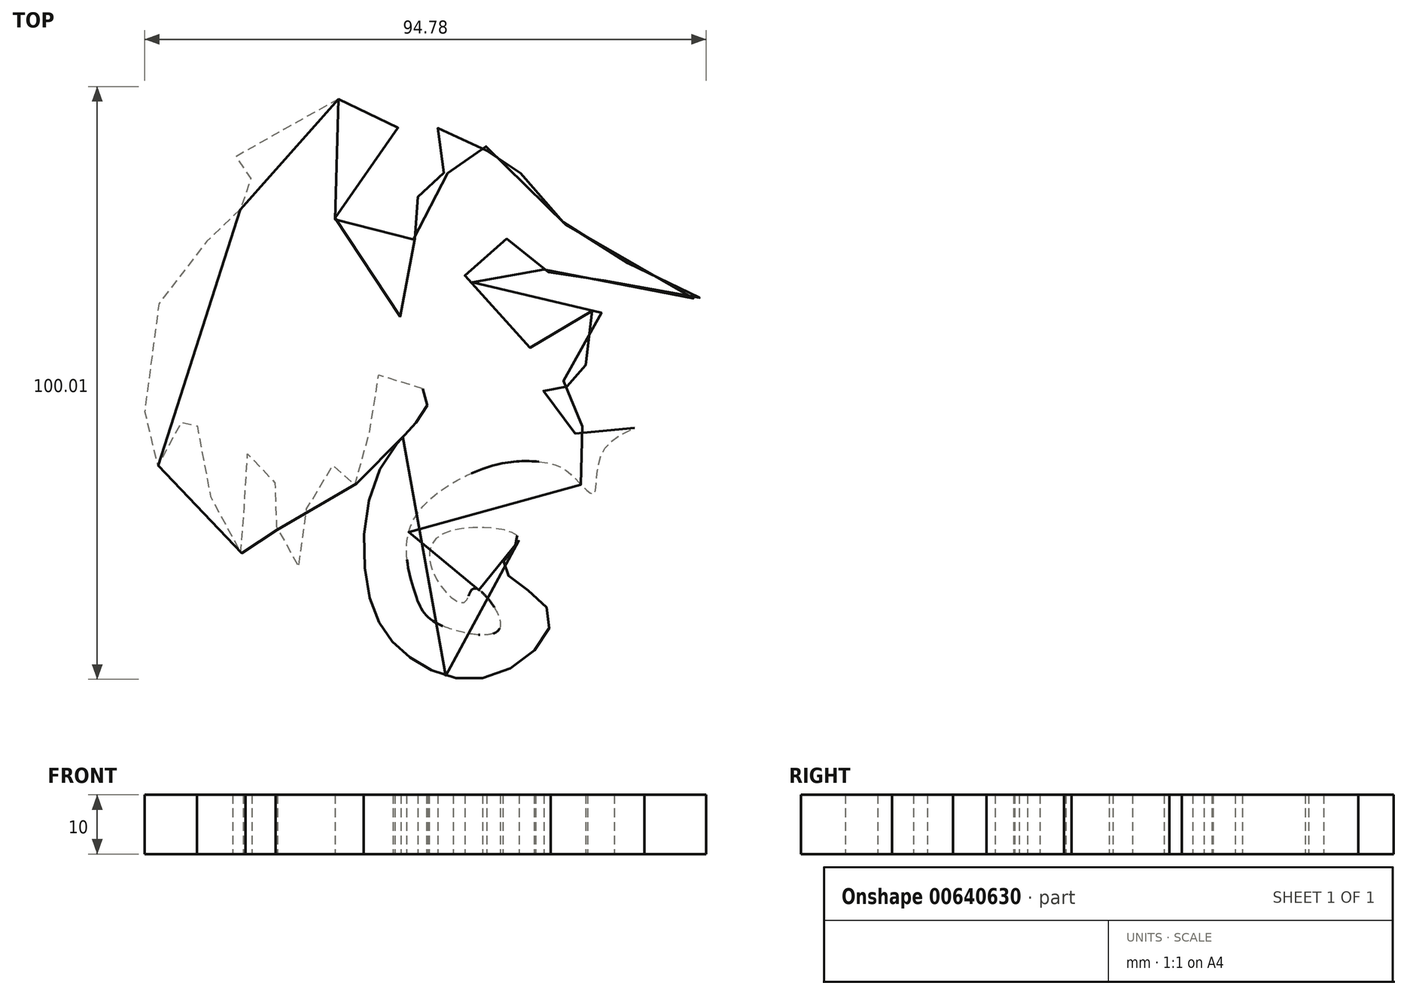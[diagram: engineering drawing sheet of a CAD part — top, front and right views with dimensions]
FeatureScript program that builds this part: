
annotation { "Feature Type Name" : "Feature", "Feature Type Description" : "" }
export const myFeature = defineFeature(function(context is Context, id is Id, definition is map)
    precondition{}
    {
        {
            var Q0;
            Q0=qCreatedBy(makeId("Top.planeOp"),FACE);
            var sketch = newSketch(context, id + "F0", { "sketchPlane" : qUnion([Q0])});
            skFitSpline(sketch, "E0", {"points": [v(-16.96, 41.65) * mm, v(-29.4, 34.76) * mm, v(-34.79, 30.9) * mm, v(-31.76, 28.22) * mm, v(-32.65, 24.68) * mm, v(-35.45, 20.64) * mm, v(-47.4, 6.83) * mm, v(-47.84, -20.41) * mm, v(-43.9, -13.53) * mm, v(-41.16, -11.67) * mm, v(-40.58, -18.2) * mm, v(-33.43, -34.97) * mm, v(-32.93, -26.4) * mm, v(-31.96, -18.08) * mm, v(-27.55, -23.55) * mm, v(-27.43, -30.59) * mm, v(-23.67, -37.29) * mm, v(-21.43, -23.3) * mm, v(-16.96, -20.52) * mm, v(-14.53, -23.54) * mm, v(-11.76, -14.81) * mm, v(-9.4, -4.4) * mm, v(-2, -8.6) * mm, v(-9.07, -19.18) * mm, v(-11.82, -42.06) * mm, v(-4.7, -52.79) * mm, v(9.25, -55.64) * mm, v(18.58, -45) * mm, v(10.74, -37.16) * mm, v(13.45, -32.45) * mm, v(0, -32.12) * mm, v(0, -40.06) * mm, v(4.38, -43.2) * mm, v(5.94, -40.96) * mm, v(10.26, -47.58) * mm, v(0, -47.02) * mm, v(-3.92, -42.22) * mm, v(-4.68, -30.08) * mm, v(8.07, -20.52) * mm, v(16.14, -19.52) * mm, v(20.95, -20.74) * mm, v(24.7, -24.22) * mm, v(26.22, -24.9) * mm, v(28.07, -17.16) * mm, v(34.62, -12.8) * mm, v(26.05, -12.46) * mm, v(21.35, -15.82) * mm, v(16.14, -13.8) * mm, v(17.65, -6.58) * mm, v(16.3, -3.72) * mm, v(19.9, -5.06) * mm, v(21.85, -7.42) * mm, v(23.7, -10.61) * mm, v(25.04, -7.92) * mm, v(25.38, 0) * mm, v(29.58, 3.67) * mm, v(25.21, 5.86) * mm, v(21.35, 2.16) * mm, v(16.64, 0) * mm, v(13.62, 0) * mm, v(7.4, 8.88) * mm, v(2.36, 14.43) * mm, v(6.22, 17.26) * mm, v(12.52, 17.4) * mm, v(13.62, 13.25) * mm, v(16.3, 13.25) * mm, v(19.64, 11.87) * mm, v(23.41, 10.99) * mm, v(26.5, 9.82) * mm, v(28.47, 11.59) * mm, v(37.48, 8.76) * mm, v(45.04, 8.71) * mm, v(39.8, 12.45) * mm, v(28.5, 14.98) * mm, v(24.74, 18.55) * mm, v(20.84, 20.98) * mm, v(19.16, 24.5) * mm, v(16.14, 25.52) * mm, v(12, 32.7) * mm, v(7.4, 37.61) * mm, v(8, 32.04) * mm, v(3.58, 35.75) * mm, v(0, 37.55) * mm, v(1.18, 33.08) * mm, v(4.34, 28.94) * mm, v(-1.84, 29.38) * mm, v(-7.72, 27.53) * mm, v(-3.7, 25.35) * mm, v(-6.44, 21.5) * mm, v(-6.86, 17.03) * mm, v(-3.19, 18.12) * mm, v(-3.19, 8.54) * mm, v(-7.55, 5.02) * mm, v(-16.8, 15.77) * mm, v(-14.28, 30.39) * mm, v(-6.88, 36.94) * mm, v(-8.23, 43.16) * mm, v(-16.96, 41.65) * mm]});
            skSolve(sketch);
        }
        {
            var Q0;
            Q0 = qSketchRegion(id + "F0", true);
            extrude(context, id + "F1", {"entities" : qUnion([Q0]), "depth" : 10 * mm, "offsetDistance" : 25 * mm});
        }
    });
